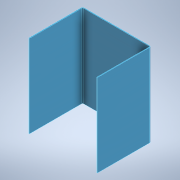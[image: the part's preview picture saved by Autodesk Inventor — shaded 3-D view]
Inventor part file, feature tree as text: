
AUTODESK INVENTOR PART (.ipt)
format: ipt  version: 2021 (Build 250183000, 183)  size: 126,976 bytes
history: native  units: mm
features: sheet_metal_op x4, sketch x2, other x2
ambient origin geometry x8: Origin, YZ Plane, XZ Plane, XY Plane, X Axis, Y Axis, Z Axis, Center Point
bodies: Solid1 (feature_tree)
feature tree (8):
  sheet_metal_op  "Face1"
  sheet_metal_op  "Flange1"
  sketch  "Sketch1"  dims[d0=102.0mm]
  other  "Plate1"
  sketch  "Sketch2"  dims[d1=123.0mm d2=61.5mm d3=51.0mm d4=1.0mm d5=1.0mm d6=0.5mm d7=2.0mm d8=1.0mm d10=90.0deg d11=1.0mm d12=4.0mm d13=1.0mm d14=1.0mm]
  other  "Plate2"
  sheet_metal_op  "Bend1"
  sheet_metal_op  "Corner1"
